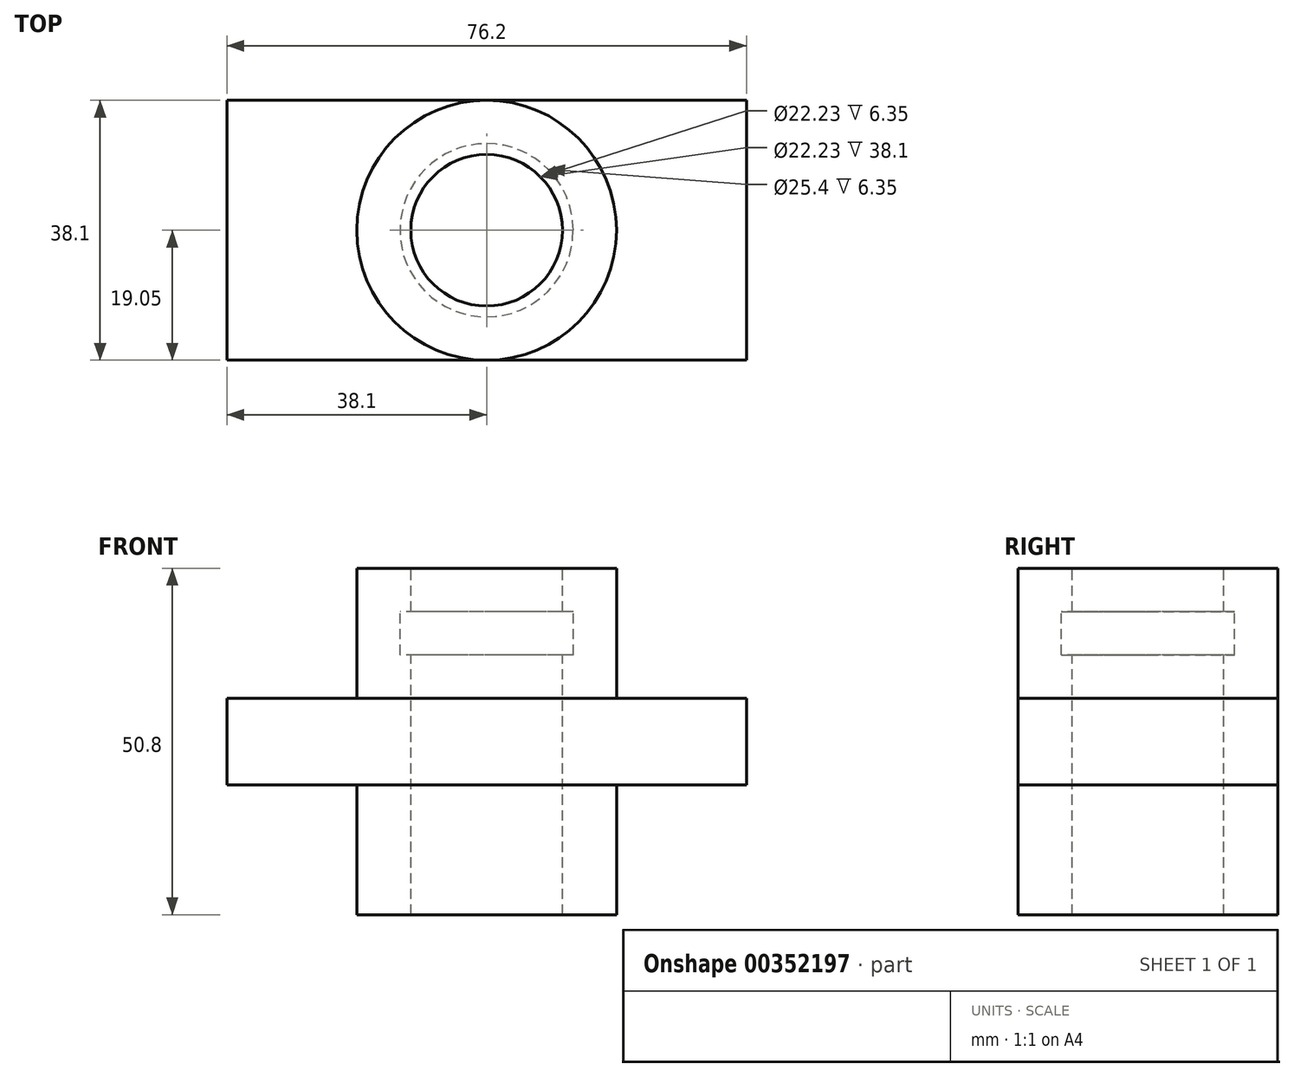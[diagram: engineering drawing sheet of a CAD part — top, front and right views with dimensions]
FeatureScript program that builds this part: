
annotation { "Feature Type Name" : "Feature", "Feature Type Description" : "" }
export const myFeature = defineFeature(function(context is Context, id is Id, definition is map)
    precondition{}
    {
        {
            var Q0;
            Q0=qCreatedBy(makeId("Front.planeOp"),FACE);
            var sketch = newSketch(context, id + "F0", { "sketchPlane" : qUnion([Q0])});
            skLineSegment(sketch, "E0", {"start": v(-19.05, 0) * mm, "end": v(19.05, 0) * mm});
            skLineSegment(sketch, "E1", {"start": v(19.05, 0) * mm, "end": v(19.05, 19.05) * mm});
            skLineSegment(sketch, "E2", {"start": v(-19.05, 0) * mm, "end": v(-19.05, 19.05) * mm});
            skLineSegment(sketch, "E3", {"start": v(-38.1, 19.05) * mm, "end": v(38.1, 19.05) * mm});
            skLineSegment(sketch, "E4", {"start": v(38.1, 19.05) * mm, "end": v(38.1, 31.75) * mm});
            skLineSegment(sketch, "E5", {"start": v(38.1, 31.75) * mm, "end": v(-38.1, 31.75) * mm});
            skLineSegment(sketch, "E6", {"start": v(-38.1, 31.75) * mm, "end": v(-38.1, 19.05) * mm});
            skLineSegment(sketch, "E7", {"start": v(-19.05, 31.75) * mm, "end": v(-19.05, 50.8) * mm});
            skLineSegment(sketch, "E8", {"start": v(-19.05, 50.8) * mm, "end": v(19.05, 50.8) * mm});
            skLineSegment(sketch, "E9", {"start": v(19.05, 50.8) * mm, "end": v(19.05, 31.75) * mm});
            skLineSegment(sketch, "E10", {"start": v(-19.05, 31.75) * mm, "end": v(-19.05, 19.05) * mm});
            skLineSegment(sketch, "E11", {"start": v(19.05, 19.05) * mm, "end": v(19.05, 31.75) * mm});
            skSolve(sketch);
        }
        {
            var Q0;
            {var subQ0=sQuery(id+"F0.wireOp",EDGE,"E7");Q0=makeQuery(id+"F0.imprint","IMPRINT",FACE,{"disambiguationData":[TD([[makeQuery(id+"F0.imprint","IMPRINT",EDGE,{"derivedFrom":subQ0}),-1.0]])]});}
            var Q1;
            {var subQ2=sQuery(id+"F0.wireOp",EDGE,"E10");Q1=makeQuery(id+"F0.imprint","IMPRINT",FACE,{"disambiguationData":[TD([[makeQuery(id+"F0.imprint","IMPRINT",EDGE,{"derivedFrom":subQ2}),1.0]])]});}
            var Q2;
            Q2=makeQuery(id+"F0.imprint","IMPRINT",FACE,{"disambiguationData":[TD([[makeQuery(id+"F0.imprint","IMPRINT",EDGE,{"derivedFrom":sQuery(id+"F0.wireOp",EDGE,"E0")}),1.0]])]});
            var Q3;
            {var subQ2=sQuery(id+"F0.wireOp",EDGE,"E6");Q3=makeQuery(id+"F0.imprint","IMPRINT",FACE,{"disambiguationData":[TD([[makeQuery(id+"F0.imprint","IMPRINT",EDGE,{"derivedFrom":subQ2}),1.0]])]});}
            var Q4;
            {var subQ2=sQuery(id+"F0.wireOp",EDGE,"E4");Q4=makeQuery(id+"F0.imprint","IMPRINT",FACE,{"disambiguationData":[TD([[makeQuery(id+"F0.imprint","IMPRINT",EDGE,{"derivedFrom":subQ2}),1.0]])]});}
            extrude(context, id + "F1", {"entities" : qUnion([Q0, Q1, Q2, Q3, Q4]), "endBound" : BoundingType.SYMMETRIC, "depth" : 38.1 * mm});
        }
        {
            var Q0;
            Q0=makeQuery(id+"F1.opExtrude","SWEPT_FACE",FACE,{"disambiguationData":[OSD([sQuery(id+"F0.wireOp",EDGE,"E8")])]});
            var sketch = newSketch(context, id + "F2", { "sketchPlane" : qUnion([Q0])});
            skCircle(sketch, "E12", {"center": v(0, 0) * mm, "radius": 19.05 * mm});
            skSolve(sketch);
        }
        {
            var Q0;
            {var subQ0=sQuery(id+"F2.wireOp",EDGE,"E12");var subQ1=sQuery(id+"F0.wireOp",EDGE,"E8");var subQ2=makeQuery(id+"F1.opExtrude","CAP_EDGE",EDGE,{"disambiguationData":[OSD([subQ1])],"isStart":true});var subQ3=makeQuery(id+"F2.imprint","INTERSECT",VERTEX,{"derivedFrom":[subQ2,subQ0]});Q0=makeQuery(id+"F2.imprint","IMPRINT",FACE,{"disambiguationData":[TD([[makeQuery(id+"F2.imprint","IMPRINT",EDGE,{"disambiguationData":[TD([[subQ3,-1.0]])],"derivedFrom":subQ0}),-1.0]])]});}
            var Q1;
            {var subQ0=sQuery(id+"F2.wireOp",EDGE,"E12");var subQ1=sQuery(id+"F0.wireOp",EDGE,"E8");var subQ2=makeQuery(id+"F1.opExtrude","CAP_EDGE",EDGE,{"disambiguationData":[OSD([subQ1])],"isStart":true});var subQ3=makeQuery(id+"F2.imprint","INTERSECT",VERTEX,{"derivedFrom":[subQ2,subQ0]});Q1=makeQuery(id+"F2.imprint","IMPRINT",FACE,{"disambiguationData":[TD([[makeQuery(id+"F2.imprint","IMPRINT",EDGE,{"disambiguationData":[TD([[subQ3,1.0]])],"derivedFrom":subQ0}),-1.0]])]});}
            var Q2;
            {var subQ0=sQuery(id+"F2.wireOp",EDGE,"E12");var subQ1=sQuery(id+"F0.wireOp",EDGE,"E8");var subQ4=makeQuery(id+"F1.opExtrude","CAP_EDGE",EDGE,{"disambiguationData":[OSD([subQ1])],"isStart":false});var subQ5=makeQuery(id+"F2.imprint","INTERSECT",VERTEX,{"derivedFrom":[subQ4,subQ0]});Q2=makeQuery(id+"F2.imprint","IMPRINT",FACE,{"disambiguationData":[TD([[makeQuery(id+"F2.imprint","IMPRINT",EDGE,{"disambiguationData":[TD([[subQ5,1.0]])],"derivedFrom":subQ0}),-1.0]])]});}
            var Q3;
            {var subQ0=sQuery(id+"F2.wireOp",EDGE,"E12");var subQ1=sQuery(id+"F0.wireOp",EDGE,"E8");var subQ4=makeQuery(id+"F1.opExtrude","CAP_EDGE",EDGE,{"disambiguationData":[OSD([subQ1])],"isStart":false});var subQ5=makeQuery(id+"F2.imprint","INTERSECT",VERTEX,{"derivedFrom":[subQ4,subQ0]});Q3=makeQuery(id+"F2.imprint","IMPRINT",FACE,{"disambiguationData":[TD([[makeQuery(id+"F2.imprint","IMPRINT",EDGE,{"disambiguationData":[TD([[subQ5,-1.0]])],"derivedFrom":subQ0}),-1.0]])]});}
            extrude(context, id + "F3", {"entities" : qUnion([Q0, Q1, Q2, Q3]), "operationType" : NewBodyOperationType.REMOVE, "oppositeDirection" : true, "depth" : 19.05 * mm});
        }
        {
            var Q0;
            Q0=makeQuery(id+"F1.opExtrude","SWEPT_FACE",FACE,{"disambiguationData":[OSD([sQuery(id+"F0.wireOp",EDGE,"E0")])]});
            var sketch = newSketch(context, id + "F4", { "sketchPlane" : qUnion([Q0])});
            skCircle(sketch, "E13", {"center": v(0, 0) * mm, "radius": 19.05 * mm});
            skSolve(sketch);
        }
        {
            var Q0;
            {var subQ0=sQuery(id+"F4.wireOp",EDGE,"E13");var subQ1=sQuery(id+"F0.wireOp",EDGE,"E0");var subQ2=makeQuery(id+"F1.opExtrude","CAP_EDGE",EDGE,{"disambiguationData":[OSD([subQ1])],"isStart":false});var subQ3=makeQuery(id+"F4.imprint","INTERSECT",VERTEX,{"derivedFrom":[subQ2,subQ0]});Q0=makeQuery(id+"F4.imprint","IMPRINT",FACE,{"disambiguationData":[TD([[makeQuery(id+"F4.imprint","IMPRINT",EDGE,{"disambiguationData":[TD([[subQ3,-1.0]])],"derivedFrom":subQ0}),-1.0]])]});}
            var Q1;
            {var subQ0=sQuery(id+"F4.wireOp",EDGE,"E13");var subQ1=sQuery(id+"F0.wireOp",EDGE,"E0");var subQ2=makeQuery(id+"F1.opExtrude","CAP_EDGE",EDGE,{"disambiguationData":[OSD([subQ1])],"isStart":false});var subQ3=makeQuery(id+"F4.imprint","INTERSECT",VERTEX,{"derivedFrom":[subQ2,subQ0]});Q1=makeQuery(id+"F4.imprint","IMPRINT",FACE,{"disambiguationData":[TD([[makeQuery(id+"F4.imprint","IMPRINT",EDGE,{"disambiguationData":[TD([[subQ3,1.0]])],"derivedFrom":subQ0}),-1.0]])]});}
            var Q2;
            {var subQ0=sQuery(id+"F4.wireOp",EDGE,"E13");var subQ1=sQuery(id+"F0.wireOp",EDGE,"E0");var subQ4=makeQuery(id+"F1.opExtrude","CAP_EDGE",EDGE,{"disambiguationData":[OSD([subQ1])],"isStart":true});var subQ5=makeQuery(id+"F4.imprint","INTERSECT",VERTEX,{"derivedFrom":[subQ4,subQ0]});Q2=makeQuery(id+"F4.imprint","IMPRINT",FACE,{"disambiguationData":[TD([[makeQuery(id+"F4.imprint","IMPRINT",EDGE,{"disambiguationData":[TD([[subQ5,-1.0]])],"derivedFrom":subQ0}),-1.0]])]});}
            var Q3;
            {var subQ0=sQuery(id+"F4.wireOp",EDGE,"E13");var subQ1=sQuery(id+"F0.wireOp",EDGE,"E0");var subQ4=makeQuery(id+"F1.opExtrude","CAP_EDGE",EDGE,{"disambiguationData":[OSD([subQ1])],"isStart":true});var subQ5=makeQuery(id+"F4.imprint","INTERSECT",VERTEX,{"derivedFrom":[subQ4,subQ0]});Q3=makeQuery(id+"F4.imprint","IMPRINT",FACE,{"disambiguationData":[TD([[makeQuery(id+"F4.imprint","IMPRINT",EDGE,{"disambiguationData":[TD([[subQ5,1.0]])],"derivedFrom":subQ0}),-1.0]])]});}
            extrude(context, id + "F5", {"entities" : qUnion([Q0, Q1, Q2, Q3]), "operationType" : NewBodyOperationType.REMOVE, "oppositeDirection" : true, "depth" : 19.05 * mm});
        }
        {
            var Q0;
            Q0=makeQuery(id+"F1.opExtrude","SWEPT_FACE",FACE,{"disambiguationData":[OSD([sQuery(id+"F0.wireOp",EDGE,"E8")])]});
            var sketch = newSketch(context, id + "F6", { "sketchPlane" : qUnion([Q0])});
            skCircle(sketch, "E14", {"center": v(0, 0) * mm, "radius": 12.7 * mm});
            skCircle(sketch, "E15", {"center": v(0, 0) * mm, "radius": 11.11 * mm});
            skSolve(sketch);
        }
        {
            var Q0;
            Q0=makeQuery(id+"F6.imprint","IMPRINT",FACE,{"disambiguationData":[TD([[makeQuery(id+"F6.imprint","IMPRINT",EDGE,{"derivedFrom":sQuery(id+"F6.wireOp",EDGE,"E14")}),1.0]])]});
            extrude(context, id + "F7", {"entities" : qUnion([Q0]), "operationType" : NewBodyOperationType.REMOVE, "oppositeDirection" : true, "depth" : 12.7 * mm, "hasSecondDirection" : true, "secondDirectionOppositeDirection" : true, "secondDirectionDepth" : 6.35 * mm});
        }
        {
            var Q0;
            Q0=makeQuery(id+"F6.imprint","IMPRINT",FACE,{"disambiguationData":[TD([[makeQuery(id+"F6.imprint","IMPRINT",EDGE,{"derivedFrom":sQuery(id+"F6.wireOp",EDGE,"E15")}),1.0]])]});
            extrude(context, id + "F8", {"entities" : qUnion([Q0]), "operationType" : NewBodyOperationType.REMOVE, "endBound" : BoundingType.THROUGH_ALL, "oppositeDirection" : true, "depth" : 25.4 * mm});
        }
    });
